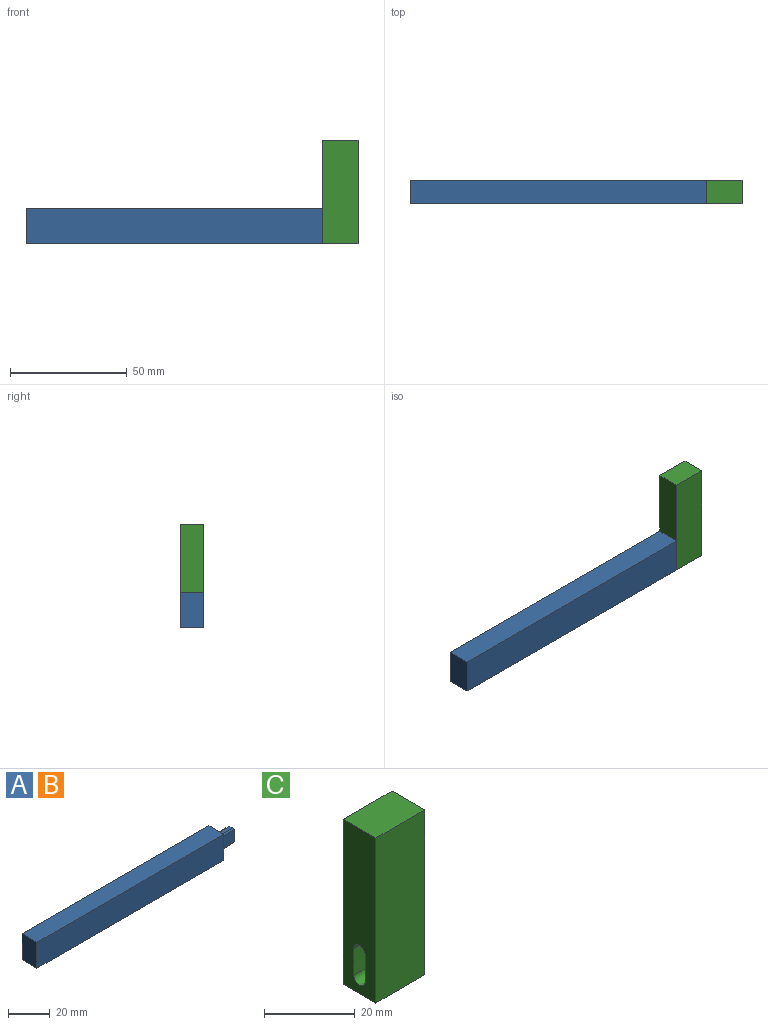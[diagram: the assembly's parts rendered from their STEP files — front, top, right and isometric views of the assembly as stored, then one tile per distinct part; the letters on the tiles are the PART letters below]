
ASSEMBLY  parts=3 mates=1
PART A: 15 faces, bbox 137.2x10.2x15.2 mm
  f0: plane 15.24x10.16mm, normal (1,0,0), area 124.6mm2, adj f2,f3,f4,f5,f6,f7,f8,f9
  f1: plane 15.24x10.16mm, normal (-1,0,0), area 154.8mm2, adj f2,f3,f4,f5
  f2: plane 127x10.16mm, normal (0,0,-1), area 1290.3mm2, adj f0,f1,f4,f5
  f3: plane 127x10.16mm, normal (0,0,1), area 1290.3mm2, adj f0,f1,f4,f5
  f4: plane 127x15.24mm, normal (0,-1,0), area 1935.5mm2, adj f0,f1,f2,f3
  f5: plane 127x15.24mm, normal (0,1,0), area 1935.5mm2, adj f0,f1,f2,f3
  f6: plane 10.16x7.11mm, normal (0,1,0), area 72.3mm2, adj f0,f7,f13,f14
  f7: cylinder r=0.76mm len=10.16mm, axis (-1,0,0), area 12.2mm2, adj f0,f6,f8,f14
  f8: plane 10.16x2.03mm, normal (0,0,1), area 20.6mm2, adj f0,f7,f9,f14
  f9: cylinder r=0.76mm len=10.16mm, axis (-1,0,0), area 12.2mm2, adj f0,f8,f10,f14
  f10: plane 10.16x7.11mm, normal (0,-1,0), area 72.3mm2, adj f0,f9,f11,f14
  f11: cylinder r=0.76mm len=10.16mm, axis (-1,0,0), area 12.2mm2, adj f0,f10,f12,f14
  f12: plane 10.16x2.03mm, normal (0,0,-1), area 20.6mm2, adj f0,f11,f13,f14
  f13: cylinder r=0.76mm len=10.16mm, axis (-1,0,0), area 12.2mm2, adj f0,f6,f12,f14
  f14: plane 8.64x3.56mm, normal (1,0,0), area 30.2mm2, adj f6,f7,f8,f9,f10,f11,f12,f13
PART B: same geometry as A
PART C: 11 faces, bbox 15.2x10.2x44.5 mm
  f0: plane 15.24x10.16mm, normal (0,0,-1), area 154.8mm2, adj f1,f3,f4,f5
  f1: plane 44.45x10.16mm, normal (1,0,0), area 451.6mm2, adj f0,f2,f4,f5
  f2: plane 15.24x10.16mm, normal (0,0,1), area 154.8mm2, adj f1,f3,f4,f5
  f3: plane 44.45x10.16mm, normal (-1,0,0), area 416.4mm2, adj f0,f2,f4,f5,f6,f7,f8,f9
  f4: plane 44.45x15.24mm, normal (0,-1,0), area 677.4mm2, adj f0,f1,f2,f3
  f5: plane 44.45x15.24mm, normal (0,1,0), area 677.4mm2, adj f0,f1,f2,f3
  f6: cylinder r=1.78mm len=10.16mm, axis (-1,0,0), area 56.8mm2, adj f3,f7,f9,f10
  f7: plane 10.16x7.11mm, normal (0,-1,0), area 72.3mm2, adj f3,f6,f8,f10
  f8: cylinder r=1.78mm len=10.16mm, axis (-1,0,0), area 56.8mm2, adj f3,f7,f9,f10
  f9: plane 10.16x7.11mm, normal (0,1,0), area 72.3mm2, adj f3,f6,f8,f10
  f10: plane 10.67x3.56mm, normal (-1,0,0), area 35.2mm2, adj f6,f7,f8,f9
PLACE A t=(-7.77,9.14,-7.62)mm
PLACE B t=(-7.77,9.14,-7.62)mm fixed
PLACE C t=(50.11,9.14,-8.02)mm
MATE fastened C.f0 <-> B.f2  axis (0,0,1) through (107.97,-1.02,-11.83)mm
